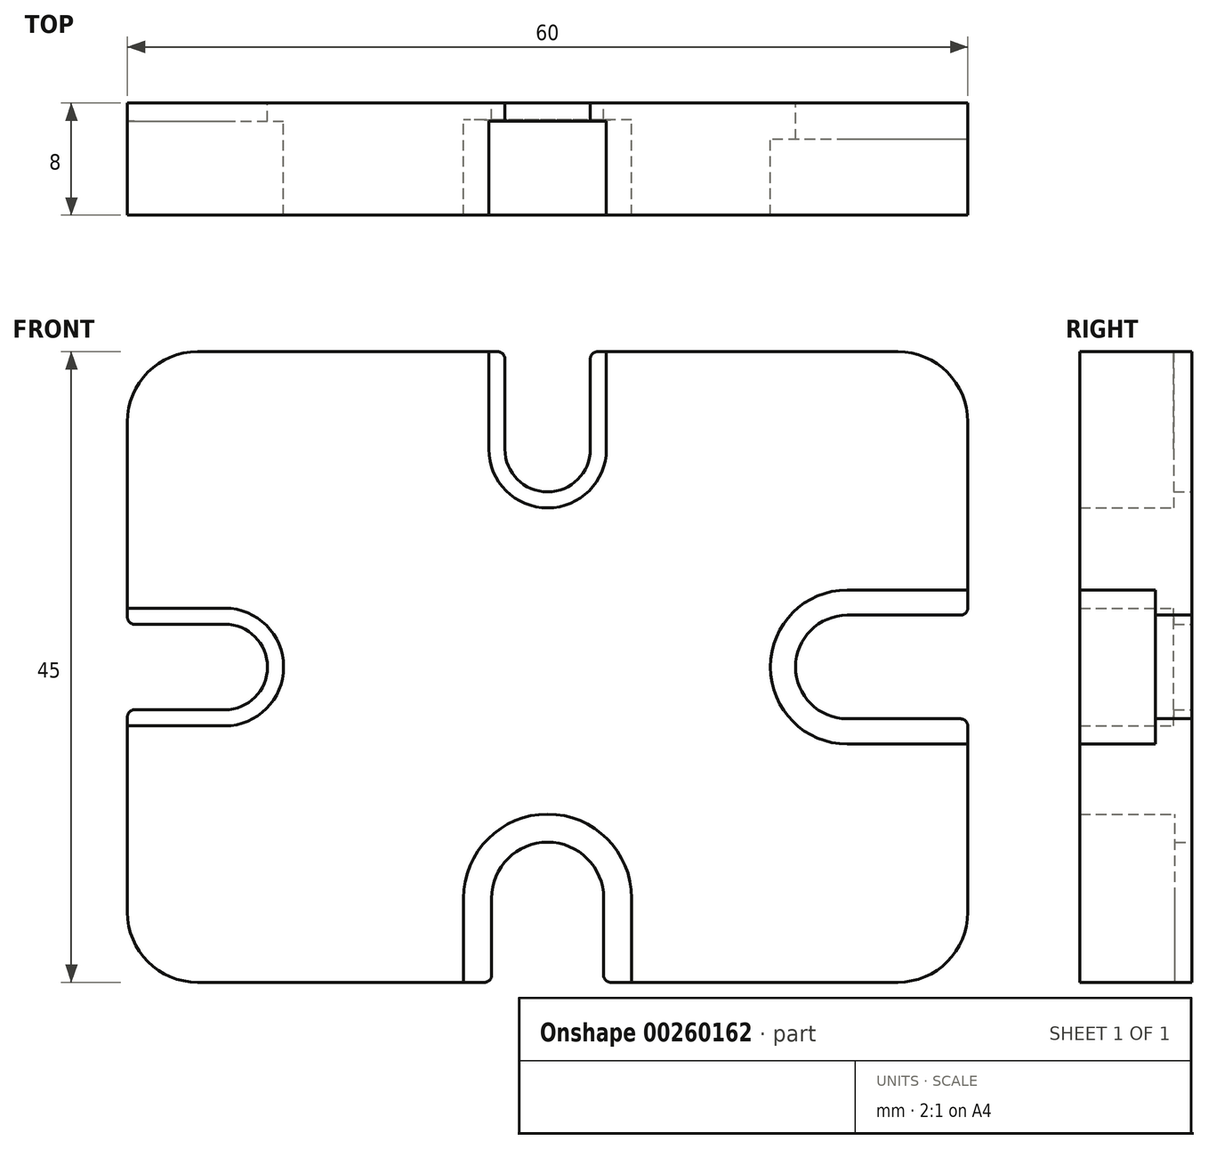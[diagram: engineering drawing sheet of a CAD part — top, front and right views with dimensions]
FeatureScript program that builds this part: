
annotation { "Feature Type Name" : "Feature", "Feature Type Description" : "" }
export const myFeature = defineFeature(function(context is Context, id is Id, definition is map)
    precondition{}
    {
        {
            var Q0;
            Q0=qCreatedBy(makeId("Front.planeOp"),FACE);
            var sketch = newSketch(context, id + "F0", { "sketchPlane" : qUnion([Q0])});
            skLineSegment(sketch, "E0.bottom", {"start": v(30, -22.5) * mm, "end": v(-30, -22.5) * mm});
            skLineSegment(sketch, "E0.top", {"start": v(30, 22.5) * mm, "end": v(-30, 22.5) * mm});
            skLineSegment(sketch, "E0.left", {"start": v(30, -22.5) * mm, "end": v(30, 22.5) * mm});
            skLineSegment(sketch, "E0.right", {"start": v(-30, -22.5) * mm, "end": v(-30, 22.5) * mm});
            skPoint(sketch, "E0.middle", {"position": v(0, 0) * mm});
            skLineSegment(sketch, "E1", {"start": v(-30, 3.05) * mm, "end": v(-23.05, 3.05) * mm});
            skArc(sketch, "E2", {"start": v(-23.05, 3.05) * mm, "mid": v(-20.9, 2.16) * mm, "end": v(-20, 0) * mm});
            skLineSegment(sketch, "E3.MirrorCS", {"start": v(-30, -3.05) * mm, "end": v(-23.05, -3.05) * mm});
            skArc(sketch, "E4.MirrorCS", {"start": v(-23.05, -3.05) * mm, "mid": v(-20.9, -2.16) * mm, "end": v(-20, 0) * mm});
            skLineSegment(sketch, "E5.0", {"start": v(-30, -4.2) * mm, "end": v(-23.05, -4.2) * mm});
            skArc(sketch, "E5.1", {"start": v(-23.05, -4.2) * mm, "mid": v(-20.08, -2.97) * mm, "end": v(-18.85, 0) * mm});
            skArc(sketch, "E5.2", {"start": v(-23.05, 4.2) * mm, "mid": v(-20.08, 2.97) * mm, "end": v(-18.85, 0) * mm});
            skLineSegment(sketch, "E5.3", {"start": v(-30, 4.2) * mm, "end": v(-23.05, 4.2) * mm});
            skLineSegment(sketch, "E6", {"start": v(30, 3.7) * mm, "end": v(21.4, 3.7) * mm});
            skArc(sketch, "E7", {"start": v(21.4, 3.7) * mm, "mid": v(18.78, 2.62) * mm, "end": v(17.7, 0) * mm});
            skLineSegment(sketch, "E8.MirrorCS", {"start": v(30, -3.7) * mm, "end": v(21.4, -3.7) * mm});
            skArc(sketch, "E9.MirrorCS", {"start": v(21.4, -3.7) * mm, "mid": v(18.78, -2.62) * mm, "end": v(17.7, 0) * mm});
            skLineSegment(sketch, "E10.0", {"start": v(30, 5.5) * mm, "end": v(21.4, 5.5) * mm});
            skArc(sketch, "E10.1", {"start": v(21.4, 5.5) * mm, "mid": v(17.51, 3.89) * mm, "end": v(15.9, 0) * mm});
            skArc(sketch, "E10.2", {"start": v(21.4, -5.5) * mm, "mid": v(17.51, -3.89) * mm, "end": v(15.9, 0) * mm});
            skLineSegment(sketch, "E10.3", {"start": v(30, -5.5) * mm, "end": v(21.4, -5.5) * mm});
            skLineSegment(sketch, "E11", {"start": v(3.05, 22.5) * mm, "end": v(3.05, 15.55) * mm});
            skArc(sketch, "E12", {"start": v(3.05, 15.55) * mm, "mid": v(2.16, 13.4) * mm, "end": v(0, 12.5) * mm});
            skArc(sketch, "E13.MirrorCS", {"start": v(-3.05, 15.55) * mm, "mid": v(-2.16, 13.4) * mm, "end": v(0, 12.5) * mm});
            skLineSegment(sketch, "E14.0", {"start": v(-4.2, 22.5) * mm, "end": v(-4.2, 15.55) * mm});
            skArc(sketch, "E14.1", {"start": v(-4.2, 15.55) * mm, "mid": v(-2.97, 12.58) * mm, "end": v(0, 11.35) * mm});
            skArc(sketch, "E14.2", {"start": v(4.2, 15.55) * mm, "mid": v(2.97, 12.58) * mm, "end": v(0, 11.35) * mm});
            skLineSegment(sketch, "E14.3", {"start": v(4.2, 22.5) * mm, "end": v(4.2, 15.55) * mm});
            skLineSegment(sketch, "E15", {"start": v(4, -22.5) * mm, "end": v(4, -16.5) * mm});
            skArc(sketch, "E16", {"start": v(4, -16.5) * mm, "mid": v(2.83, -13.67) * mm, "end": v(0, -12.5) * mm});
            skLineSegment(sketch, "E17.MirrorCS", {"start": v(-4, -22.5) * mm, "end": v(-4, -16.5) * mm});
            skArc(sketch, "E18.MirrorCS", {"start": v(-4, -16.5) * mm, "mid": v(-2.83, -13.67) * mm, "end": v(0, -12.5) * mm});
            skLineSegment(sketch, "E19.0", {"start": v(6, -22.5) * mm, "end": v(6, -16.5) * mm});
            skArc(sketch, "E19.1", {"start": v(6, -16.5) * mm, "mid": v(4.24, -12.26) * mm, "end": v(0, -10.5) * mm});
            skArc(sketch, "E19.2", {"start": v(-6, -16.5) * mm, "mid": v(-4.24, -12.26) * mm, "end": v(0, -10.5) * mm});
            skLineSegment(sketch, "E19.3", {"start": v(-6, -22.5) * mm, "end": v(-6, -16.5) * mm});
            skLineSegment(sketch, "E20", {"start": v(-3.05, 15.55) * mm, "end": v(-3.05, 22.5) * mm});
            skSolve(sketch);
        }
        {
            var Q0;
            {var subQ15=sQuery(id+"F0.wireOp",EDGE,"E5.0");Q0=makeQuery(id+"F0.imprint","IMPRINT",FACE,{"disambiguationData":[TD([[makeQuery(id+"F0.imprint","IMPRINT",EDGE,{"derivedFrom":subQ15}),-1.0]])]});}
            extrude(context, id + "F1", {"entities" : qUnion([Q0]), "depth" : 8 * mm});
        }
        {
            var Q0;
            {var subQ0=sQuery(id+"F0.wireOp",EDGE,"E1");Q0=makeQuery(id+"F0.imprint","IMPRINT",FACE,{"disambiguationData":[TD([[makeQuery(id+"F0.imprint","IMPRINT",EDGE,{"derivedFrom":subQ0}),1.0]])]});}
            extrude(context, id + "F2", {"entities" : qUnion([Q0]), "operationType" : NewBodyOperationType.ADD, "depth" : 1.3 * mm});
        }
        {
            var Q0;
            {var subQ0=sQuery(id+"F0.wireOp",EDGE,"E6");Q0=makeQuery(id+"F0.imprint","IMPRINT",FACE,{"disambiguationData":[TD([[makeQuery(id+"F0.imprint","IMPRINT",EDGE,{"derivedFrom":subQ0}),-1.0]])]});}
            extrude(context, id + "F3", {"entities" : qUnion([Q0]), "operationType" : NewBodyOperationType.ADD, "depth" : 2.6 * mm});
        }
        {
            var Q0;
            {var subQ3=sQuery(id+"F0.wireOp",EDGE,"E11");Q0=makeQuery(id+"F0.imprint","IMPRINT",FACE,{"disambiguationData":[TD([[makeQuery(id+"F0.imprint","IMPRINT",EDGE,{"derivedFrom":subQ3}),1.0]])]});}
            extrude(context, id + "F4", {"entities" : qUnion([Q0]), "operationType" : NewBodyOperationType.ADD, "depth" : 1.3 * mm});
        }
        {
            var Q0;
            {var subQ0=sQuery(id+"F0.wireOp",EDGE,"E15");Q0=makeQuery(id+"F0.imprint","IMPRINT",FACE,{"disambiguationData":[TD([[makeQuery(id+"F0.imprint","IMPRINT",EDGE,{"derivedFrom":subQ0}),-1.0]])]});}
            extrude(context, id + "F5", {"entities" : qUnion([Q0]), "operationType" : NewBodyOperationType.ADD, "depth" : 1.2 * mm});
        }
        {
            var Q0;
            Q0=makeQuery(id+"F1.opExtrude","SWEPT_EDGE",EDGE,{"disambiguationData":[OSD([sQuery(id+"F0.wireOp",EDGE,"E0.top"),sQuery(id+"F0.wireOp",EDGE,"E0.right")])]});
            var Q1;
            Q1=makeQuery(id+"F1.opExtrude","SWEPT_EDGE",EDGE,{"disambiguationData":[OSD([sQuery(id+"F0.wireOp",EDGE,"E0.top"),sQuery(id+"F0.wireOp",EDGE,"E0.left")])]});
            var Q2;
            Q2=makeQuery(id+"F1.opExtrude","SWEPT_EDGE",EDGE,{"disambiguationData":[OSD([sQuery(id+"F0.wireOp",EDGE,"E0.bottom"),sQuery(id+"F0.wireOp",EDGE,"E0.right")])]});
            var Q3;
            Q3=makeQuery(id+"F1.opExtrude","SWEPT_EDGE",EDGE,{"disambiguationData":[OSD([sQuery(id+"F0.wireOp",EDGE,"E0.bottom"),sQuery(id+"F0.wireOp",EDGE,"E0.left")])]});
            fillet(context, id + "F6", {"entities" : qUnion([Q0, Q1, Q2, Q3]), "radius" : 5 * mm, "tangentPropagation" : true, "allowEdgeOverflow" : false});
        }
        {
            var Q0;
            Q0=makeQuery(id+"F2.opExtrude","SWEPT_EDGE",EDGE,{"disambiguationData":[OSD([sQuery(id+"F0.wireOp",EDGE,"E0.right"),sQuery(id+"F0.wireOp",EDGE,"E1")])]});
            var Q1;
            Q1=makeQuery(id+"F2.opExtrude","SWEPT_EDGE",EDGE,{"disambiguationData":[OSD([sQuery(id+"F0.wireOp",EDGE,"E0.right"),sQuery(id+"F0.wireOp",EDGE,"E3.MirrorCS")])]});
            var Q2;
            Q2=makeQuery(id+"F3.opExtrude","SWEPT_EDGE",EDGE,{"disambiguationData":[OSD([sQuery(id+"F0.wireOp",EDGE,"E0.left"),sQuery(id+"F0.wireOp",EDGE,"E6")])]});
            var Q3;
            Q3=makeQuery(id+"F3.opExtrude","SWEPT_EDGE",EDGE,{"disambiguationData":[OSD([sQuery(id+"F0.wireOp",EDGE,"E0.left"),sQuery(id+"F0.wireOp",EDGE,"E8.MirrorCS")])]});
            var Q4;
            Q4=makeQuery(id+"F5.opExtrude","SWEPT_EDGE",EDGE,{"disambiguationData":[OSD([sQuery(id+"F0.wireOp",EDGE,"E0.bottom"),sQuery(id+"F0.wireOp",EDGE,"E15")])]});
            var Q5;
            Q5=makeQuery(id+"F5.opExtrude","SWEPT_EDGE",EDGE,{"disambiguationData":[OSD([sQuery(id+"F0.wireOp",EDGE,"E0.bottom"),sQuery(id+"F0.wireOp",EDGE,"E17.MirrorCS")])]});
            var Q6;
            Q6=makeQuery(id+"F4.opExtrude","SWEPT_EDGE",EDGE,{"disambiguationData":[OSD([sQuery(id+"F0.wireOp",EDGE,"E0.top"),sQuery(id+"F0.wireOp",EDGE,"E11")])]});
            var Q7;
            Q7=makeQuery(id+"F4.opExtrude","SWEPT_EDGE",EDGE,{"disambiguationData":[OSD([sQuery(id+"F0.wireOp",EDGE,"E0.top"),sQuery(id+"F0.wireOp",EDGE,"5c21a501-26c6-4e62-9abe-04da3597ee65.MirrorCS")])]});
            fillet(context, id + "F7", {"entities" : qUnion([Q0, Q1, Q2, Q3, Q4, Q5, Q6, Q7]), "radius" : 0.5 * mm, "tangentPropagation" : true, "allowEdgeOverflow" : false});
        }
    });
